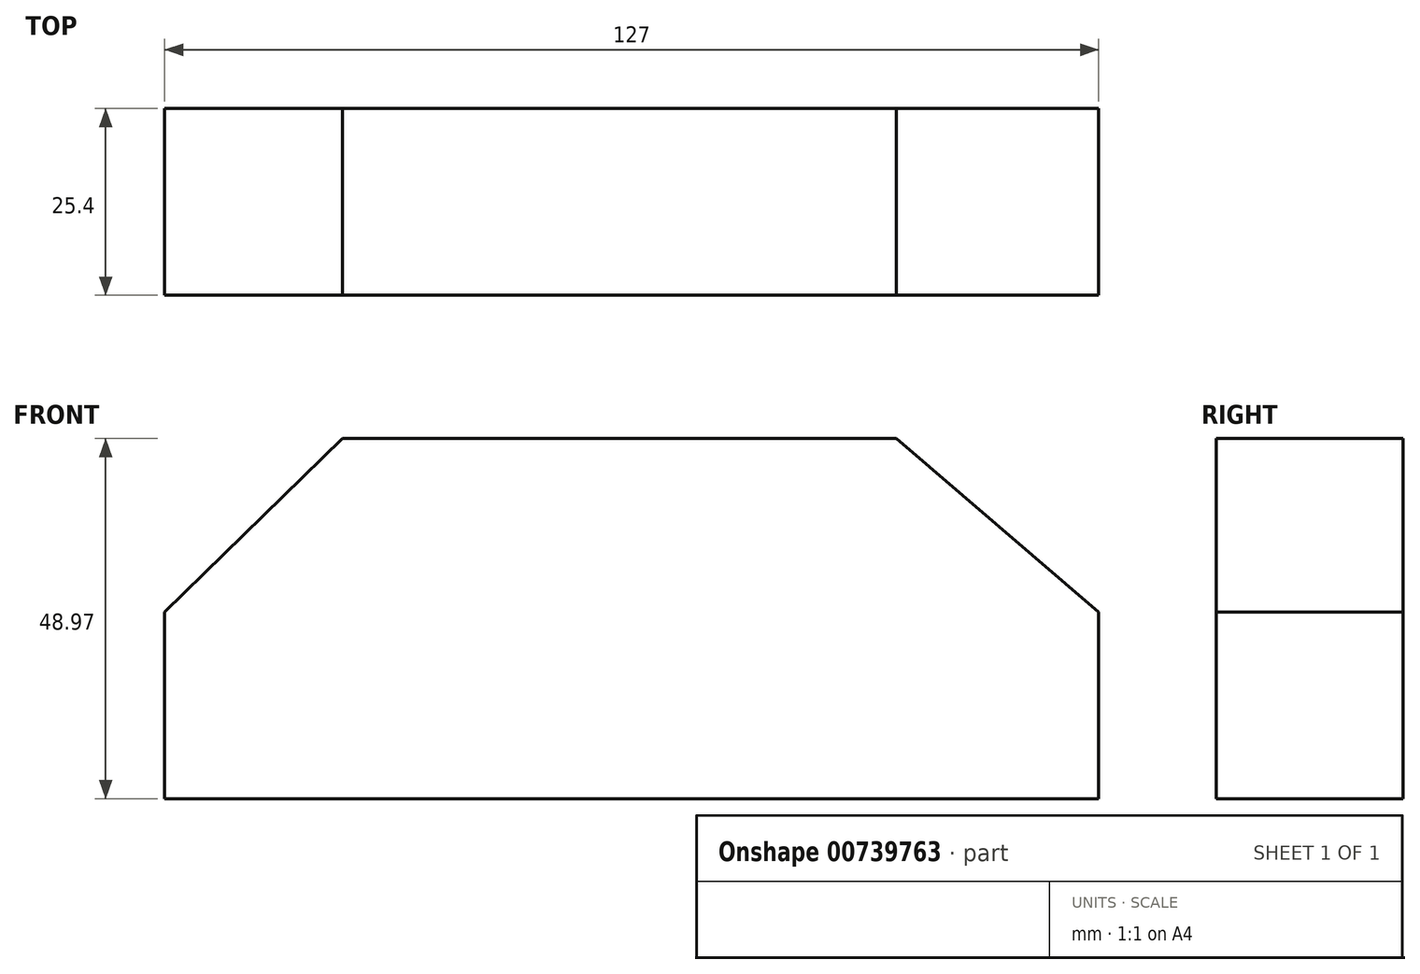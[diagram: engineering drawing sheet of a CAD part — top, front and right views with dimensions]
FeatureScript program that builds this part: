
annotation { "Feature Type Name" : "Feature", "Feature Type Description" : "" }
export const myFeature = defineFeature(function(context is Context, id is Id, definition is map)
    precondition{}
    {
        {
            var Q0;
            Q0=qCreatedBy(makeId("Front.planeOp"),FACE);
            var sketch = newSketch(context, id + "F0", { "sketchPlane" : qUnion([Q0])});
            skLineSegment(sketch, "E0", {"start": v(-60.61, -13.79) * mm, "end": v(-60.61, 11.61) * mm});
            skLineSegment(sketch, "E1", {"start": v(-60.61, 11.61) * mm, "end": v(-36.44, 35.18) * mm});
            skLineSegment(sketch, "E2", {"start": v(-36.44, 35.18) * mm, "end": v(38.87, 35.18) * mm});
            skLineSegment(sketch, "E3", {"start": v(38.87, 35.18) * mm, "end": v(66.39, 11.61) * mm});
            skLineSegment(sketch, "E4", {"start": v(66.39, 11.61) * mm, "end": v(66.39, -13.79) * mm});
            skLineSegment(sketch, "E5", {"start": v(66.39, -13.79) * mm, "end": v(-60.61, -13.79) * mm});
            skSolve(sketch);
        }
        {
            var Q0;
            Q0 = qSketchRegion(id + "F0", true);
            extrude(context, id + "F1", {"entities" : qUnion([Q0]), "depth" : 25.4 * mm, "offsetDistance" : 25.4 * mm});
        }
    });
